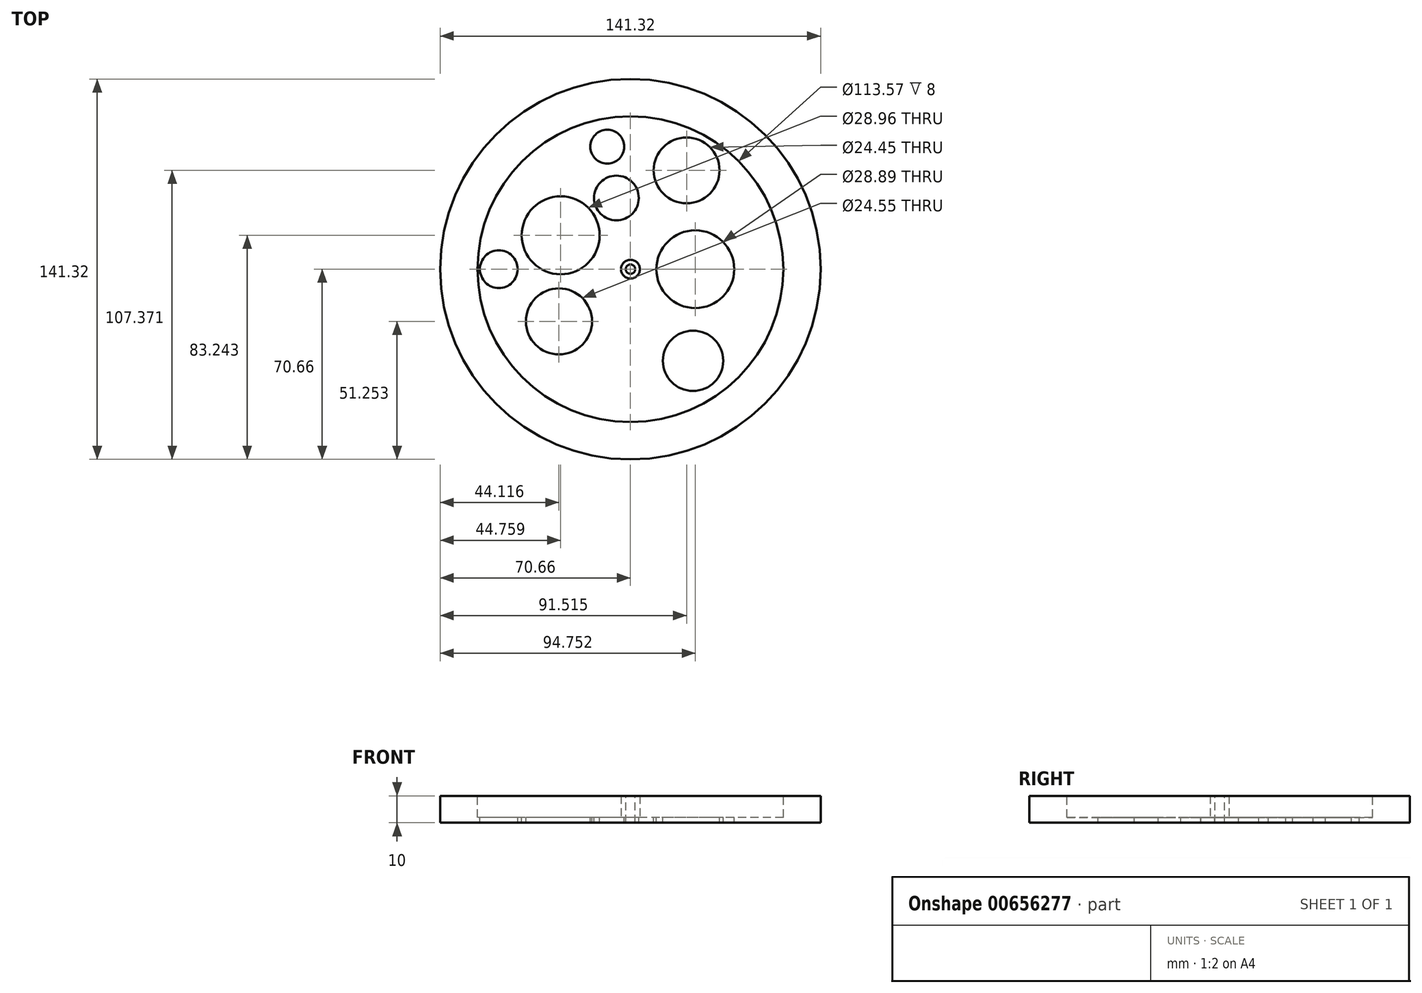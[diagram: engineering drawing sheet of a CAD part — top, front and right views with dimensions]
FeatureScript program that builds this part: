
annotation { "Feature Type Name" : "Feature", "Feature Type Description" : "" }
export const myFeature = defineFeature(function(context is Context, id is Id, definition is map)
    precondition{}
    {
        {
            var Q0;
            Q0=qCreatedBy(makeId("Top.planeOp"),FACE);
            var sketch = newSketch(context, id + "F0", { "sketchPlane" : qUnion([Q0])});
            skCircle(sketch, "E0", {"center": v(0, 0) * mm, "radius": 70.66 * mm});
            skSolve(sketch);
        }
        {
            var Q0;
            Q0=makeQuery(id+"F0.imprint","IMPRINT",FACE,{"disambiguationData":[TD([[makeQuery(id+"F0.imprint","IMPRINT",EDGE,{"derivedFrom":sQuery(id+"F0.wireOp",EDGE,"E0")}),1.0]])]});
            extrude(context, id + "F1", {"entities" : qUnion([Q0]), "depth" : 10 * mm, "offsetDistance" : 25.4 * mm});
        }
        {
            var Q0;
            Q0=makeQuery(id+"F1.opExtrude","CAP_FACE",FACE,{"disambiguationData":[OSD([sQuery(id+"F0.wireOp",EDGE,"E0")])],"isStart":false});
            var sketch = newSketch(context, id + "F2", { "sketchPlane" : qUnion([Q0])});
            skCircle(sketch, "E1", {"center": v(0, 0) * mm, "radius": 56.78 * mm});
            skSolve(sketch);
        }
        {
            var Q0;
            Q0=makeQuery(id+"F2.imprint","IMPRINT",FACE,{"disambiguationData":[TD([[makeQuery(id+"F2.imprint","IMPRINT",EDGE,{"derivedFrom":sQuery(id+"F2.wireOp",EDGE,"E1")}),1.0]])]});
            extrude(context, id + "F3", {"entities" : qUnion([Q0]), "operationType" : NewBodyOperationType.REMOVE, "oppositeDirection" : true, "depth" : 8 * mm, "offsetDistance" : 25.4 * mm});
        }
        {
            var Q0;
            Q0=makeQuery(id+"F3.boolean.opBoolean","COPY",FACE,{"derivedFrom":makeQuery(id+"F3.opExtrude","CAP_FACE",FACE,{"disambiguationData":[OSD([sQuery(id+"F2.wireOp",EDGE,"E1")])],"isStart":false})});
            var sketch = newSketch(context, id + "F4", { "sketchPlane" : qUnion([Q0])});
            skCircle(sketch, "E2", {"center": v(-25.9, 12.58) * mm, "radius": 14.48 * mm});
            skSolve(sketch);
        }
        {
            var Q0;
            Q0 = qSketchRegion(id + "F4", true);
            extrude(context, id + "F5", {"entities" : qUnion([Q0]), "operationType" : NewBodyOperationType.REMOVE, "oppositeDirection" : true, "depth" : 8 * mm, "offsetDistance" : 25.4 * mm});
        }
        {
            var Q0;
            Q0=makeQuery(id+"F3.boolean.opBoolean","COPY",FACE,{"derivedFrom":makeQuery(id+"F3.opExtrude","CAP_FACE",FACE,{"disambiguationData":[OSD([sQuery(id+"F2.wireOp",EDGE,"E1")])],"isStart":false})});
            var sketch = newSketch(context, id + "F6", { "sketchPlane" : qUnion([Q0])});
            skCircle(sketch, "E3", {"center": v(20.85, 36.71) * mm, "radius": 12.23 * mm});
            skSolve(sketch);
        }
        {
            var Q0;
            Q0 = qSketchRegion(id + "F6", true);
            extrude(context, id + "F7", {"entities" : qUnion([Q0]), "operationType" : NewBodyOperationType.REMOVE, "oppositeDirection" : true, "depth" : 8 * mm, "offsetDistance" : 25.4 * mm});
        }
        {
            var Q0;
            Q0=makeQuery(id+"F3.boolean.opBoolean","COPY",FACE,{"derivedFrom":makeQuery(id+"F3.opExtrude","CAP_FACE",FACE,{"disambiguationData":[OSD([sQuery(id+"F2.wireOp",EDGE,"E1")])],"isStart":false})});
            var sketch = newSketch(context, id + "F8", { "sketchPlane" : qUnion([Q0])});
            skCircle(sketch, "E4", {"center": v(-48.9, 0) * mm, "radius": 7.01 * mm});
            skSolve(sketch);
        }
        {
            var Q0;
            Q0 = qSketchRegion(id + "F8", true);
            extrude(context, id + "F9", {"entities" : qUnion([Q0]), "operationType" : NewBodyOperationType.REMOVE, "oppositeDirection" : true, "depth" : 8 * mm, "offsetDistance" : 25.4 * mm});
        }
        {
            var Q0;
            Q0=makeQuery(id+"F3.boolean.opBoolean","COPY",FACE,{"derivedFrom":makeQuery(id+"F3.opExtrude","CAP_FACE",FACE,{"disambiguationData":[OSD([sQuery(id+"F2.wireOp",EDGE,"E1")])],"isStart":false})});
            var sketch = newSketch(context, id + "F10", { "sketchPlane" : qUnion([Q0])});
            skCircle(sketch, "E5", {"center": v(24.1, 0) * mm, "radius": 14.44 * mm});
            skSolve(sketch);
        }
        {
            var Q0;
            Q0 = qSketchRegion(id + "F10", true);
            extrude(context, id + "F11", {"entities" : qUnion([Q0]), "operationType" : NewBodyOperationType.REMOVE, "oppositeDirection" : true, "depth" : 8 * mm, "offsetDistance" : 25.4 * mm});
        }
        {
            var Q0;
            Q0=makeQuery(id+"F3.boolean.opBoolean","COPY",FACE,{"derivedFrom":makeQuery(id+"F3.opExtrude","CAP_FACE",FACE,{"disambiguationData":[OSD([sQuery(id+"F2.wireOp",EDGE,"E1")])],"isStart":false})});
            var sketch = newSketch(context, id + "F12", { "sketchPlane" : qUnion([Q0])});
            skCircle(sketch, "E6", {"center": v(0, 0) * mm, "radius": 3.5 * mm});
            skSolve(sketch);
        }
        {
            var Q0;
            Q0=makeQuery(id+"F3.boolean.opBoolean","COPY",FACE,{"derivedFrom":makeQuery(id+"F3.opExtrude","CAP_FACE",FACE,{"disambiguationData":[OSD([sQuery(id+"F2.wireOp",EDGE,"E1")])],"isStart":false})});
            var sketch = newSketch(context, id + "F13", { "sketchPlane" : qUnion([Q0])});
            skCircle(sketch, "E7", {"center": v(-8.6, 45.51) * mm, "radius": 6.3 * mm});
            skSolve(sketch);
        }
        {
            var Q0;
            Q0 = qSketchRegion(id + "F13", true);
            extrude(context, id + "F14", {"entities" : qUnion([Q0]), "operationType" : NewBodyOperationType.REMOVE, "oppositeDirection" : true, "depth" : 8 * mm, "offsetDistance" : 25.4 * mm});
        }
        {
            var Q0;
            Q0=makeQuery(id+"F3.boolean.opBoolean","COPY",FACE,{"derivedFrom":makeQuery(id+"F3.opExtrude","CAP_FACE",FACE,{"disambiguationData":[OSD([sQuery(id+"F2.wireOp",EDGE,"E1")])],"isStart":false})});
            var sketch = newSketch(context, id + "F15", { "sketchPlane" : qUnion([Q0])});
            skCircle(sketch, "E8", {"center": v(-5.23, 26.43) * mm, "radius": 8.32 * mm});
            skSolve(sketch);
        }
        {
            var Q0;
            Q0 = qSketchRegion(id + "F15", true);
            extrude(context, id + "F16", {"entities" : qUnion([Q0]), "operationType" : NewBodyOperationType.REMOVE, "oppositeDirection" : true, "depth" : 8 * mm, "offsetDistance" : 25.4 * mm});
        }
        {
            var Q0;
            Q0=qCreatedBy(makeId("Top.planeOp"),FACE);
            var sketch = newSketch(context, id + "F17", { "sketchPlane" : qUnion([Q0])});
            skCircle(sketch, "E9", {"center": v(14.56, -20.26) * mm, "radius": 6.03 * mm});
            skSolve(sketch);
        }
        {
            var Q0;
            Q0 = qSketchRegion(id + "F17", true);
            extrude(context, id + "F18", {"entities" : qUnion([Q0]), "operationType" : NewBodyOperationType.REMOVE, "oppositeDirection" : true, "depth" : 8 * mm, "offsetDistance" : 25.4 * mm});
        }
        {
            var Q0;
            Q0=makeQuery(id+"F3.boolean.opBoolean","COPY",FACE,{"derivedFrom":makeQuery(id+"F3.opExtrude","CAP_FACE",FACE,{"disambiguationData":[OSD([sQuery(id+"F2.wireOp",EDGE,"E1")])],"isStart":false})});
            var sketch = newSketch(context, id + "F19", { "sketchPlane" : qUnion([Q0])});
            skCircle(sketch, "E10", {"center": v(23.25, -34.04) * mm, "radius": 11.2 * mm});
            skSolve(sketch);
        }
        {
            var Q0;
            Q0=makeQuery(id+"F19.imprint","IMPRINT",FACE,{"disambiguationData":[TD([[makeQuery(id+"F19.imprint","IMPRINT",EDGE,{"derivedFrom":sQuery(id+"F19.wireOp",EDGE,"E10")}),1.0]])]});
            extrude(context, id + "F20", {"entities" : qUnion([Q0]), "operationType" : NewBodyOperationType.REMOVE, "oppositeDirection" : true, "depth" : 8 * mm, "offsetDistance" : 25.4 * mm});
        }
        {
            var Q0;
            Q0=makeQuery(id+"F12.imprint","IMPRINT",FACE,{"disambiguationData":[TD([[makeQuery(id+"F12.imprint","IMPRINT",EDGE,{"derivedFrom":sQuery(id+"F12.wireOp",EDGE,"E6")}),1.0]])]});
            extrude(context, id + "F21", {"entities" : qUnion([Q0]), "operationType" : NewBodyOperationType.ADD, "depth" : 8 * mm, "offsetDistance" : 25.4 * mm});
        }
        {
            var Q0;
            Q0=makeQuery(id+"F21.opExtrude","CAP_FACE",FACE,{"disambiguationData":[OSD([sQuery(id+"F12.wireOp",EDGE,"E6")])],"isStart":false});
            var sketch = newSketch(context, id + "F22", { "sketchPlane" : qUnion([Q0])});
            skPoint(sketch, "E11", {"position": v(0, 0) * mm});
            skSolve(sketch);
        }
        {
            var Q0;
            Q0=sQuery(id+"F22.wireOp",VERTEX,"E11");
            var Q1;
            Q1=makeQuery(id+"F1.opExtrude","SWEPT_BODY",BODY,{"disambiguationData":[OSD([sQuery(id+"F0.wireOp",EDGE,"E0")])]});
            hole(context, id + "F23", {"style" : HoleStyle.SIMPLE, "endStyle" : HoleEndStyle.THROUGH, "holeDiameter" : 3.5 * mm, "majorDiameter" : 6.35 * mm, "isTappedThrough" : true, "tappedDepth" : 12.7 * mm, "tapClearance" : 3, "locations" : qUnion([Q0]), "scope" : qUnion([Q1])});
        }
        {
            var Q0;
            Q0=makeQuery(id+"F3.boolean.opBoolean","COPY",FACE,{"derivedFrom":makeQuery(id+"F3.opExtrude","CAP_FACE",FACE,{"disambiguationData":[OSD([sQuery(id+"F2.wireOp",EDGE,"E1")])],"isStart":false})});
            var sketch = newSketch(context, id + "F24", { "sketchPlane" : qUnion([Q0])});
            skCircle(sketch, "E12", {"center": v(-26.54, -19.4) * mm, "radius": 12.27 * mm});
            skSolve(sketch);
        }
        {
            var Q0;
            Q0=makeQuery(id+"F24.imprint","IMPRINT",FACE,{"disambiguationData":[TD([[makeQuery(id+"F24.imprint","IMPRINT",EDGE,{"derivedFrom":sQuery(id+"F24.wireOp",EDGE,"E12")}),1.0]])]});
            var Q1;
            Q1=sQuery(id+"F24.wireOp",EDGE,"E12");
            extrude(context, id + "F25", {"entities" : qUnion([Q0]), "operationType" : NewBodyOperationType.REMOVE, "surfaceEntities" : qUnion([Q1]), "oppositeDirection" : true, "depth" : 8 * mm, "offsetDistance" : 25.4 * mm});
        }
    });
